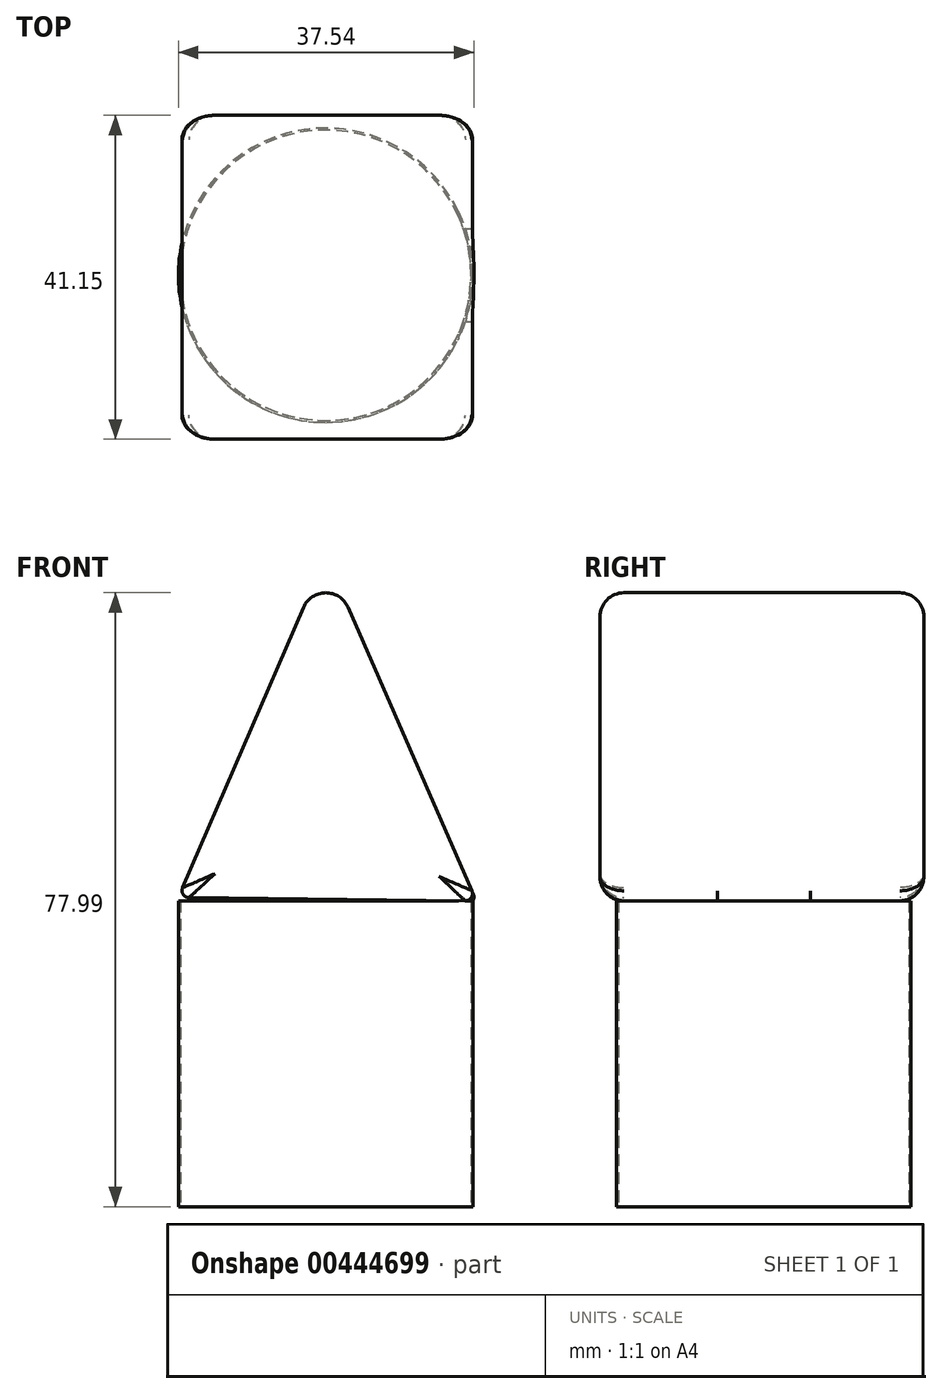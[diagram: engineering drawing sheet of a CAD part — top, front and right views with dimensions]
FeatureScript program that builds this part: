
annotation { "Feature Type Name" : "Feature", "Feature Type Description" : "" }
export const myFeature = defineFeature(function(context is Context, id is Id, definition is map)
    precondition{}
    {
        {
            var Q0;
            Q0=qCreatedBy(makeId("Top.planeOp"),FACE);
            var sketch = newSketch(context, id + "F0", { "sketchPlane" : qUnion([Q0])});
            skCircle(sketch, "E0", {"center": v(0, 0) * mm, "radius": 18.7 * mm});
            skSolve(sketch);
        }
        {
            var Q0;
            Q0 = qSketchRegion(id + "F0", true);
            extrude(context, id + "F1", {"entities" : qUnion([Q0]), "depth" : 28.96 * mm, "hasSecondDirection" : true, "secondDirectionOppositeDirection" : true, "secondDirectionDepth" : 9.9 * mm});
        }
        {
            var Q0;
            Q0=qCreatedBy(makeId("Top.planeOp"),FACE);
            var sketch = newSketch(context, id + "F2", { "sketchPlane" : qUnion([Q0])});
            skCircle(sketch, "E1", {"center": v(0, 0) * mm, "radius": 18.45 * mm});
            skSolve(sketch);
        }
        {
            var Q0;
            Q0 = qSketchRegion(id + "F2", true);
            extrude(context, id + "F3", {"entities" : qUnion([Q0]), "operationType" : NewBodyOperationType.REMOVE, "depth" : 29.46 * mm, "hasSecondDirection" : true, "secondDirectionOppositeDirection" : true, "secondDirectionDepth" : 25.4 * mm});
        }
        {
            var Q0;
            Q0=qCreatedBy(makeId("Front.planeOp"),FACE);
            var sketch = newSketch(context, id + "F4", { "sketchPlane" : qUnion([Q0])});
            skLineSegment(sketch, "E2", {"start": v(-18.7, 29.37) * mm, "end": v(0, 72.7) * mm});
            skLineSegment(sketch, "E3", {"start": v(0, 72.7) * mm, "end": v(19.14, 28.93) * mm});
            skLineSegment(sketch, "E4", {"start": v(19.14, 28.93) * mm, "end": v(-18.7, 29.37) * mm});
            skSolve(sketch);
        }
        {
            var Q0;
            Q0 = qSketchRegion(id + "F4", true);
            extrude(context, id + "F5", {"entities" : qUnion([Q0]), "operationType" : NewBodyOperationType.ADD, "depth" : 20.83 * mm, "hasSecondDirection" : true, "secondDirectionOppositeDirection" : true, "secondDirectionDepth" : 20.32 * mm});
        }
        {
            var Q0;
            Q0=makeQuery(id+"F5.opExtrude","SWEPT_EDGE",EDGE,{"disambiguationData":[OSD([sQuery(id+"F4.wireOp",EDGE,"E2"),sQuery(id+"F4.wireOp",EDGE,"E3")])]});
            var Q1;
            Q1=makeQuery(id+"F5.opExtrude","CAP_EDGE",EDGE,{"disambiguationData":[OSD([sQuery(id+"F4.wireOp",EDGE,"E3")])],"isStart":false});
            var Q2;
            Q2=makeQuery(id+"F5.opExtrude","CAP_EDGE",EDGE,{"disambiguationData":[OSD([sQuery(id+"F4.wireOp",EDGE,"E4")])],"isStart":true});
            var Q3;
            Q3=makeQuery(id+"F5.opExtrude","CAP_EDGE",EDGE,{"disambiguationData":[OSD([sQuery(id+"F4.wireOp",EDGE,"E4")])],"isStart":false});
            var Q4;
            Q4=makeQuery(id+"F5.opExtrude","CAP_EDGE",EDGE,{"disambiguationData":[OSD([sQuery(id+"F4.wireOp",EDGE,"E2")])],"isStart":true});
            var Q5;
            Q5=makeQuery(id+"F5.opExtrude","CAP_EDGE",EDGE,{"disambiguationData":[OSD([sQuery(id+"F4.wireOp",EDGE,"E3")])],"isStart":true});
            var Q6;
            Q6=makeQuery(id+"F5.opExtrude","CAP_EDGE",EDGE,{"disambiguationData":[OSD([sQuery(id+"F4.wireOp",EDGE,"E2")])],"isStart":false});
            fillet(context, id + "F6", {"entities" : qUnion([Q0, Q1, Q2, Q3, Q4, Q5, Q6]), "radius" : 3.07 * mm, "tangentPropagation" : true, "allowEdgeOverflow" : false});
        }
        {
            var Q0;
            Q0=makeQuery(id+"F5.opExtrude","SWEPT_EDGE",EDGE,{"disambiguationData":[OSD([sQuery(id+"F4.wireOp",EDGE,"E2"),sQuery(id+"F4.wireOp",EDGE,"E4")])]});
            var Q1;
            Q1=makeQuery(id+"F5.opExtrude","SWEPT_EDGE",EDGE,{"disambiguationData":[OSD([sQuery(id+"F4.wireOp",EDGE,"E3"),sQuery(id+"F4.wireOp",EDGE,"E4")])]});
            fillet(context, id + "F7", {"entities" : qUnion([Q0, Q1]), "radius" : 0.9 * mm, "tangentPropagation" : true, "allowEdgeOverflow" : false});
        }
    });
